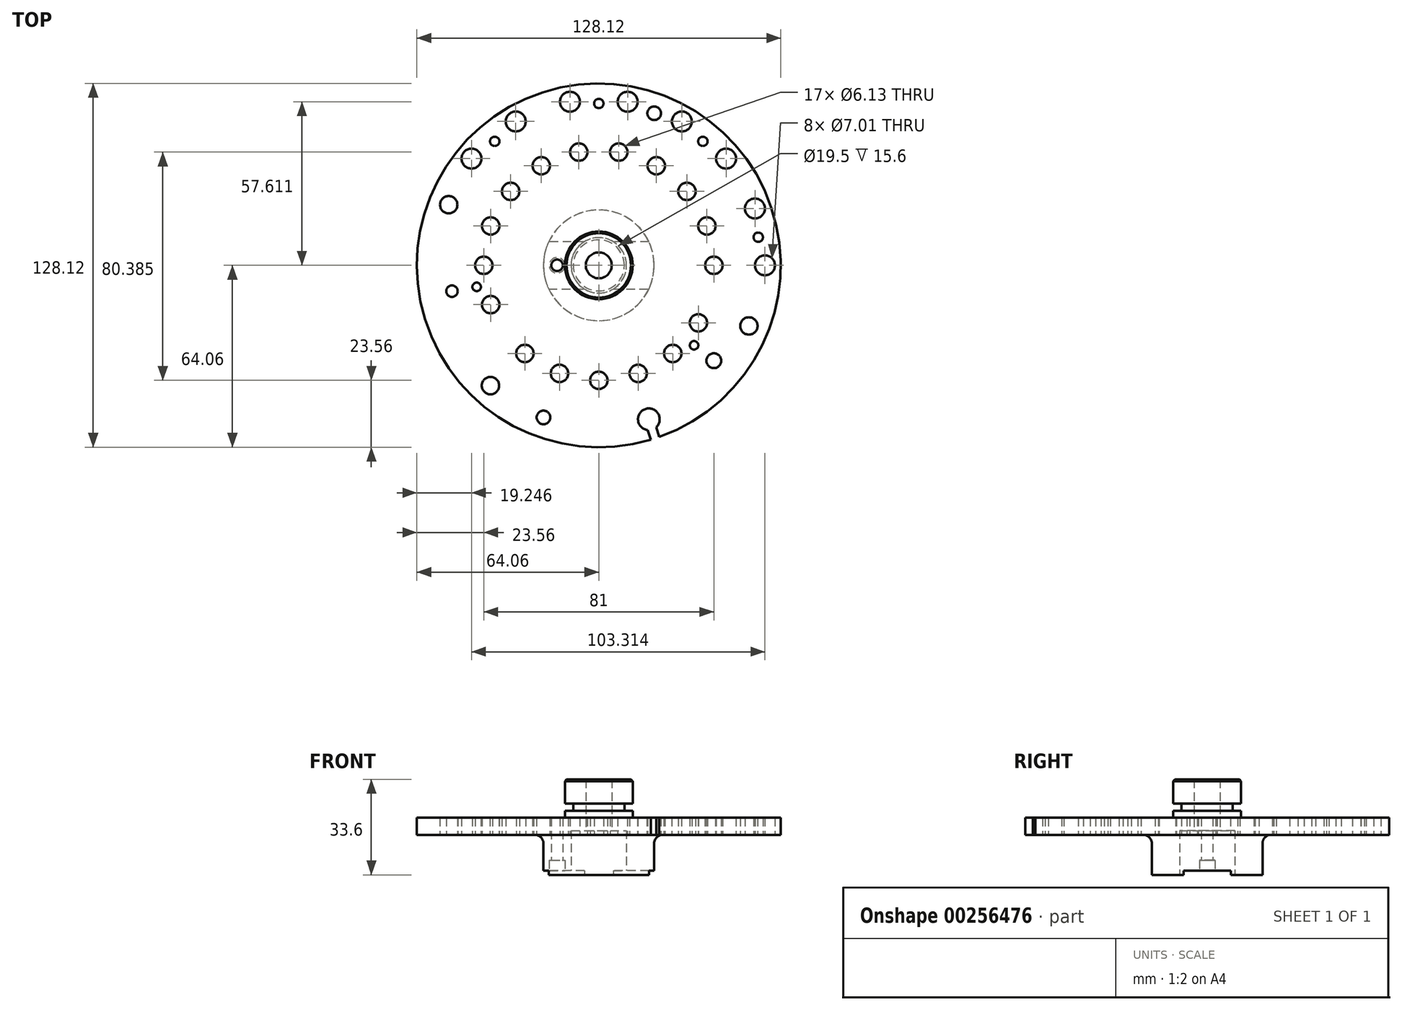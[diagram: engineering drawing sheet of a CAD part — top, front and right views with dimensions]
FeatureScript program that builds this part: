
annotation { "Feature Type Name" : "Feature", "Feature Type Description" : "" }
export const myFeature = defineFeature(function(context is Context, id is Id, definition is map)
    precondition{}
    {
        {
            var Q0;
            Q0=qCreatedBy(makeId("Front.planeOp"),FACE);
            var sketch = newSketch(context, id + "F0", { "sketchPlane" : qUnion([Q0])});
            skLineSegment(sketch, "E0", {"start": v(3.25, 0) * mm, "end": v(6.5, 0) * mm});
            skLineSegment(sketch, "E1", {"start": v(6.5, 0) * mm, "end": v(6.5, 4.7) * mm});
            skLineSegment(sketch, "E2", {"start": v(6.5, 4.7) * mm, "end": v(21.35, 4.7) * mm});
            skLineSegment(sketch, "E3", {"start": v(21.35, 4.7) * mm, "end": v(21.35, 6.7) * mm});
            skLineSegment(sketch, "E4", {"start": v(21.35, 6.7) * mm, "end": v(3.98, 6.7) * mm});
            skLineSegment(sketch, "E5", {"start": v(3.98, 6.7) * mm, "end": v(3.98, 7.5) * mm});
            skLineSegment(sketch, "E6", {"start": v(3.98, 11.2) * mm, "end": v(1.52, 11.2) * mm});
            skLineSegment(sketch, "E7", {"start": v(1.52, 11.2) * mm, "end": v(1.52, 5.2) * mm});
            skLineSegment(sketch, "E8", {"start": v(1.52, 5.2) * mm, "end": v(3.25, 5.2) * mm});
            skLineSegment(sketch, "E9", {"start": v(3.25, 5.2) * mm, "end": v(3.25, 0) * mm});
            skLineSegment(sketch, "E10", {"start": v(3.98, 7.5) * mm, "end": v(3, 7.5) * mm});
            skLineSegment(sketch, "E11", {"start": v(3, 7.5) * mm, "end": v(3, 8.35) * mm});
            skLineSegment(sketch, "E12", {"start": v(3, 8.35) * mm, "end": v(3.98, 8.35) * mm});
            skLineSegment(sketch, "E13", {"start": v(3.98, 8.35) * mm, "end": v(3.98, 11.2) * mm});
            skLineSegment(sketch, "E14", {"start": v(0, 0) * mm, "end": v(0, 11.2) * mm, "construction": true});
            skSolve(sketch);
        }
        {
            var Q0;
            Q0=makeQuery(id+"F0.imprint","IMPRINT",FACE,{"disambiguationData":[TD([[makeQuery(id+"F0.imprint","IMPRINT",EDGE,{"derivedFrom":sQuery(id+"F0.wireOp",EDGE,"E0")}),1.0]])]});
            var Q1;
            Q1=sQuery(id+"F0.wireOp",EDGE,"E14");
            revolve(context, id + "F1", {"entities" : qUnion([Q0]), "axis" : qUnion([Q1]), "revolveType" : RevolveType.FULL});
        }
        {
            var Q0;
            Q0=makeQuery(id+"F1.opRevolve","SWEPT_FACE",FACE,{"disambiguationData":[OSD([sQuery(id+"F0.wireOp",EDGE,"E2")])]});
            var sketch = newSketch(context, id + "F2", { "sketchPlane" : qUnion([Q0])});
            skLineSegment(sketch, "E15", {"start": v(21.35, 0) * mm, "end": v(0, 0) * mm, "construction": true});
            skLineSegment(sketch, "E16", {"start": v(0, 0) * mm, "end": v(20.07, -7.3) * mm, "construction": true});
            skLineSegment(sketch, "E17", {"start": v(0, 0) * mm, "end": v(16.36, -13.73) * mm, "construction": true});
            skLineSegment(sketch, "E18", {"start": v(0, 0) * mm, "end": v(10.68, -18.5) * mm, "construction": true});
            skLineSegment(sketch, "E19", {"start": v(0, 0) * mm, "end": v(3.7, -21.03) * mm, "construction": true});
            skLineSegment(sketch, "E20", {"start": v(0, 0) * mm, "end": v(-3.7, -21.03) * mm, "construction": true});
            skLineSegment(sketch, "E21", {"start": v(0, 0) * mm, "end": v(-10.68, -18.5) * mm, "construction": true});
            skLineSegment(sketch, "E22", {"start": v(0, 0) * mm, "end": v(-16.36, -13.73) * mm, "construction": true});
            skLineSegment(sketch, "E23", {"start": v(0, 0) * mm, "end": v(-20.07, -7.3) * mm, "construction": true});
            skLineSegment(sketch, "E24", {"start": v(0, 0) * mm, "end": v(-21.35, 0) * mm, "construction": true});
            skLineSegment(sketch, "E25", {"start": v(0, 0) * mm, "end": v(-20.07, 7.3) * mm, "construction": true});
            skLineSegment(sketch, "E26", {"start": v(0, 0) * mm, "end": v(18.5, 10.68) * mm, "construction": true});
            skLineSegment(sketch, "E27", {"start": v(0, 0) * mm, "end": v(13.73, 16.36) * mm, "construction": true});
            skLineSegment(sketch, "E28", {"start": v(0, 0) * mm, "end": v(7.3, 20.07) * mm, "construction": true});
            skLineSegment(sketch, "E29", {"start": v(0, 0) * mm, "end": v(0, 21.35) * mm, "construction": true});
            skLineSegment(sketch, "E30", {"start": v(0, 0) * mm, "end": v(-7.3, 20.07) * mm, "construction": true});
            skLineSegment(sketch, "E31", {"start": v(0, 0) * mm, "end": v(-13.73, 16.36) * mm, "construction": true});
            skCircle(sketch, "E32", {"center": v(0, 0) * mm, "radius": 19.5 * mm, "construction": true});
            skCircle(sketch, "E33", {"center": v(0, 0) * mm, "radius": 13.5 * mm, "construction": true});
            skCircle(sketch, "E34", {"center": v(19.5, 0) * mm, "radius": 1.17 * mm});
            skCircle(sketch, "E35", {"center": v(18.32, -6.67) * mm, "radius": 1.17 * mm});
            skCircle(sketch, "E36", {"center": v(14.94, -12.53) * mm, "radius": 1.17 * mm});
            skCircle(sketch, "E37", {"center": v(9.75, -16.89) * mm, "radius": 1.17 * mm});
            skCircle(sketch, "E38", {"center": v(3.39, -19.2) * mm, "radius": 1.17 * mm});
            skCircle(sketch, "E39", {"center": v(-3.39, -19.2) * mm, "radius": 1.17 * mm});
            skCircle(sketch, "E40", {"center": v(-9.75, -16.89) * mm, "radius": 1.17 * mm});
            skCircle(sketch, "E41", {"center": v(-14.94, -12.53) * mm, "radius": 1.17 * mm});
            skCircle(sketch, "E42", {"center": v(-17.62, -7.12) * mm, "radius": 1.02 * mm});
            skCircle(sketch, "E43", {"center": v(11.7, 6.75) * mm, "radius": 1.02 * mm});
            skCircle(sketch, "E44", {"center": v(8.68, 10.34) * mm, "radius": 1.02 * mm});
            skCircle(sketch, "E45", {"center": v(12.69, -4.62) * mm, "radius": 1.02 * mm});
            skCircle(sketch, "E46", {"center": v(13.5, 0) * mm, "radius": 1.02 * mm});
            skCircle(sketch, "E47", {"center": v(10.34, -8.68) * mm, "radius": 1.02 * mm});
            skCircle(sketch, "E48", {"center": v(6.75, -11.7) * mm, "radius": 1.02 * mm});
            skCircle(sketch, "E49", {"center": v(2.34, -13.3) * mm, "radius": 1.02 * mm});
            skCircle(sketch, "E50", {"center": v(-2.34, -13.3) * mm, "radius": 1.02 * mm});
            skCircle(sketch, "E51", {"center": v(-6.75, -11.7) * mm, "radius": 1.02 * mm});
            skCircle(sketch, "E52", {"center": v(-10.34, -8.68) * mm, "radius": 1.02 * mm});
            skCircle(sketch, "E53", {"center": v(-12.69, -4.62) * mm, "radius": 1.02 * mm});
            skCircle(sketch, "E54", {"center": v(-13.5, 0) * mm, "radius": 1.02 * mm});
            skCircle(sketch, "E55", {"center": v(-12.69, 4.62) * mm, "radius": 1.02 * mm});
            skCircle(sketch, "E56", {"center": v(-8.68, 10.34) * mm, "radius": 1.02 * mm});
            skCircle(sketch, "E57", {"center": v(-4.62, 12.69) * mm, "radius": 1.02 * mm});
            skCircle(sketch, "E58", {"center": v(0, 13.5) * mm, "radius": 1.02 * mm});
            skCircle(sketch, "E59", {"center": v(4.62, 12.69) * mm, "radius": 1.02 * mm});
            skLineSegment(sketch, "E60", {"start": v(0, 0) * mm, "end": v(21.03, -3.7) * mm, "construction": true});
            skLineSegment(sketch, "E61", {"start": v(0, 0) * mm, "end": v(13.73, -16.36) * mm, "construction": true});
            skLineSegment(sketch, "E62", {"start": v(0, 0) * mm, "end": v(7.3, -20.07) * mm, "construction": true});
            skLineSegment(sketch, "E63", {"start": v(0, 0) * mm, "end": v(0, -21.35) * mm, "construction": true});
            skLineSegment(sketch, "E64", {"start": v(0, 0) * mm, "end": v(-13.73, -16.36) * mm, "construction": true});
            skCircle(sketch, "E65", {"center": v(18.71, -3.3) * mm, "radius": 0.55 * mm});
            skCircle(sketch, "E66", {"center": v(12.21, -14.55) * mm, "radius": 0.55 * mm});
            skCircle(sketch, "E67", {"center": v(0, -19) * mm, "radius": 0.55 * mm});
            skCircle(sketch, "E68", {"center": v(-12.21, -14.55) * mm, "radius": 0.55 * mm});
            skCircle(sketch, "E69", {"center": v(6.5, -17.85) * mm, "radius": 0.8 * mm});
            skCircle(sketch, "E70", {"center": v(0, 0) * mm, "radius": 19 * mm, "construction": true});
            skLineSegment(sketch, "E71", {"start": v(0, 0) * mm, "end": v(17.62, 7.12) * mm, "construction": true});
            skCircle(sketch, "E72", {"center": v(17.62, 7.12) * mm, "radius": 1.02 * mm});
            skLineSegment(sketch, "E73", {"start": v(0, 0) * mm, "end": v(5.87, 18.07) * mm, "construction": true});
            skArc(sketch, "E74", {"start": v(5.73, 19.33) * mm, "mid": v(5.48, 16.86) * mm, "end": v(6.72, 19.01) * mm});
            skLineSegment(sketch, "E75", {"start": v(5.73, 19.33) * mm, "end": v(6.1, 20.46) * mm});
            skLineSegment(sketch, "E76", {"start": v(6.72, 19.01) * mm, "end": v(7.1, 20.14) * mm});
            skCircle(sketch, "E77", {"center": v(13.5, 11.2) * mm, "radius": 0.87 * mm});
            skCircle(sketch, "E78", {"center": v(11.18, 9.38) * mm, "radius": 0.5 * mm});
            skLineSegment(sketch, "E79", {"start": v(11.18, 9.38) * mm, "end": v(0, 0) * mm, "construction": true});
            skCircle(sketch, "E80", {"center": v(-6.5, 17.85) * mm, "radius": 0.8 * mm});
            skCircle(sketch, "E81", {"center": v(-12.71, 14.12) * mm, "radius": 1.02 * mm});
            skLineSegment(sketch, "E82", {"start": v(0, 0) * mm, "end": v(-12.71, 14.12) * mm, "construction": true});
            skLineSegment(sketch, "E83", {"start": v(0, 0) * mm, "end": v(-17.23, 3.04) * mm, "construction": true});
            skPoint(sketch, "E84", {"position": v(-14.33, 2.53) * mm});
            skCircle(sketch, "E85", {"center": v(-17.23, 3.04) * mm, "radius": 0.68 * mm});
            skCircle(sketch, "E86", {"center": v(-14.33, 2.53) * mm, "radius": 0.5 * mm});
            skLineSegment(sketch, "E87", {"start": v(0, 0) * mm, "end": v(-17.62, -7.12) * mm, "construction": true});
            skSolve(sketch);
        }
        {
            var Q0;
            {Q0=qUnion([makeQuery(id+"F2.imprint","IMPRINT",FACE,{"disambiguationData":[TD([[makeQuery(id+"F2.imprint","IMPRINT",EDGE,{"derivedFrom":sQuery(id+"F2.wireOp",EDGE,"E34")}),1.0]])]}),makeQuery(id+"F2.imprint","IMPRINT",FACE,{"disambiguationData":[TD([[makeQuery(id+"F2.imprint","IMPRINT",EDGE,{"derivedFrom":sQuery(id+"F2.wireOp",EDGE,"E35")}),1.0]])]}),makeQuery(id+"F2.imprint","IMPRINT",FACE,{"disambiguationData":[TD([[makeQuery(id+"F2.imprint","IMPRINT",EDGE,{"derivedFrom":sQuery(id+"F2.wireOp",EDGE,"E36")}),1.0]])]}),makeQuery(id+"F2.imprint","IMPRINT",FACE,{"disambiguationData":[TD([[makeQuery(id+"F2.imprint","IMPRINT",EDGE,{"derivedFrom":sQuery(id+"F2.wireOp",EDGE,"E37")}),1.0]])]}),makeQuery(id+"F2.imprint","IMPRINT",FACE,{"disambiguationData":[TD([[makeQuery(id+"F2.imprint","IMPRINT",EDGE,{"derivedFrom":sQuery(id+"F2.wireOp",EDGE,"E38")}),1.0]])]}),makeQuery(id+"F2.imprint","IMPRINT",FACE,{"disambiguationData":[TD([[makeQuery(id+"F2.imprint","IMPRINT",EDGE,{"derivedFrom":sQuery(id+"F2.wireOp",EDGE,"E39")}),1.0]])]}),makeQuery(id+"F2.imprint","IMPRINT",FACE,{"disambiguationData":[TD([[makeQuery(id+"F2.imprint","IMPRINT",EDGE,{"derivedFrom":sQuery(id+"F2.wireOp",EDGE,"E40")}),1.0]])]}),makeQuery(id+"F2.imprint","IMPRINT",FACE,{"disambiguationData":[TD([[makeQuery(id+"F2.imprint","IMPRINT",EDGE,{"derivedFrom":sQuery(id+"F2.wireOp",EDGE,"E41")}),1.0]])]}),makeQuery(id+"F2.imprint","IMPRINT",FACE,{"disambiguationData":[TD([[makeQuery(id+"F2.imprint","IMPRINT",EDGE,{"derivedFrom":sQuery(id+"F2.wireOp",EDGE,"E42")}),1.0]])]}),makeQuery(id+"F2.imprint","IMPRINT",FACE,{"disambiguationData":[TD([[makeQuery(id+"F2.imprint","IMPRINT",EDGE,{"derivedFrom":sQuery(id+"F2.wireOp",EDGE,"E43")}),1.0]])]}),makeQuery(id+"F2.imprint","IMPRINT",FACE,{"disambiguationData":[TD([[makeQuery(id+"F2.imprint","IMPRINT",EDGE,{"derivedFrom":sQuery(id+"F2.wireOp",EDGE,"E44")}),1.0]])]}),makeQuery(id+"F2.imprint","IMPRINT",FACE,{"disambiguationData":[TD([[makeQuery(id+"F2.imprint","IMPRINT",EDGE,{"derivedFrom":sQuery(id+"F2.wireOp",EDGE,"E45")}),1.0]])]}),makeQuery(id+"F2.imprint","IMPRINT",FACE,{"disambiguationData":[TD([[makeQuery(id+"F2.imprint","IMPRINT",EDGE,{"derivedFrom":sQuery(id+"F2.wireOp",EDGE,"E46")}),1.0]])]}),makeQuery(id+"F2.imprint","IMPRINT",FACE,{"disambiguationData":[TD([[makeQuery(id+"F2.imprint","IMPRINT",EDGE,{"derivedFrom":sQuery(id+"F2.wireOp",EDGE,"E47")}),1.0]])]}),makeQuery(id+"F2.imprint","IMPRINT",FACE,{"disambiguationData":[TD([[makeQuery(id+"F2.imprint","IMPRINT",EDGE,{"derivedFrom":sQuery(id+"F2.wireOp",EDGE,"E48")}),1.0]])]}),makeQuery(id+"F2.imprint","IMPRINT",FACE,{"disambiguationData":[TD([[makeQuery(id+"F2.imprint","IMPRINT",EDGE,{"derivedFrom":sQuery(id+"F2.wireOp",EDGE,"E49")}),1.0]])]}),makeQuery(id+"F2.imprint","IMPRINT",FACE,{"disambiguationData":[TD([[makeQuery(id+"F2.imprint","IMPRINT",EDGE,{"derivedFrom":sQuery(id+"F2.wireOp",EDGE,"E50")}),1.0]])]}),makeQuery(id+"F2.imprint","IMPRINT",FACE,{"disambiguationData":[TD([[makeQuery(id+"F2.imprint","IMPRINT",EDGE,{"derivedFrom":sQuery(id+"F2.wireOp",EDGE,"E51")}),1.0]])]}),makeQuery(id+"F2.imprint","IMPRINT",FACE,{"disambiguationData":[TD([[makeQuery(id+"F2.imprint","IMPRINT",EDGE,{"derivedFrom":sQuery(id+"F2.wireOp",EDGE,"E52")}),1.0]])]}),makeQuery(id+"F2.imprint","IMPRINT",FACE,{"disambiguationData":[TD([[makeQuery(id+"F2.imprint","IMPRINT",EDGE,{"derivedFrom":sQuery(id+"F2.wireOp",EDGE,"E53")}),1.0]])]}),makeQuery(id+"F2.imprint","IMPRINT",FACE,{"disambiguationData":[TD([[makeQuery(id+"F2.imprint","IMPRINT",EDGE,{"derivedFrom":sQuery(id+"F2.wireOp",EDGE,"E54")}),1.0]])]}),makeQuery(id+"F2.imprint","IMPRINT",FACE,{"disambiguationData":[TD([[makeQuery(id+"F2.imprint","IMPRINT",EDGE,{"derivedFrom":sQuery(id+"F2.wireOp",EDGE,"E55")}),1.0]])]}),makeQuery(id+"F2.imprint","IMPRINT",FACE,{"disambiguationData":[TD([[makeQuery(id+"F2.imprint","IMPRINT",EDGE,{"derivedFrom":sQuery(id+"F2.wireOp",EDGE,"E56")}),1.0]])]}),makeQuery(id+"F2.imprint","IMPRINT",FACE,{"disambiguationData":[TD([[makeQuery(id+"F2.imprint","IMPRINT",EDGE,{"derivedFrom":sQuery(id+"F2.wireOp",EDGE,"E57")}),1.0]])]}),makeQuery(id+"F2.imprint","IMPRINT",FACE,{"disambiguationData":[TD([[makeQuery(id+"F2.imprint","IMPRINT",EDGE,{"derivedFrom":sQuery(id+"F2.wireOp",EDGE,"E58")}),1.0]])]}),makeQuery(id+"F2.imprint","IMPRINT",FACE,{"disambiguationData":[TD([[makeQuery(id+"F2.imprint","IMPRINT",EDGE,{"derivedFrom":sQuery(id+"F2.wireOp",EDGE,"E59")}),1.0]])]}),makeQuery(id+"F2.imprint","IMPRINT",FACE,{"disambiguationData":[TD([[makeQuery(id+"F2.imprint","IMPRINT",EDGE,{"derivedFrom":sQuery(id+"F2.wireOp",EDGE,"E65")}),1.0]])]}),makeQuery(id+"F2.imprint","IMPRINT",FACE,{"disambiguationData":[TD([[makeQuery(id+"F2.imprint","IMPRINT",EDGE,{"derivedFrom":sQuery(id+"F2.wireOp",EDGE,"E66")}),1.0]])]}),makeQuery(id+"F2.imprint","IMPRINT",FACE,{"disambiguationData":[TD([[makeQuery(id+"F2.imprint","IMPRINT",EDGE,{"derivedFrom":sQuery(id+"F2.wireOp",EDGE,"E67")}),1.0]])]}),makeQuery(id+"F2.imprint","IMPRINT",FACE,{"disambiguationData":[TD([[makeQuery(id+"F2.imprint","IMPRINT",EDGE,{"derivedFrom":sQuery(id+"F2.wireOp",EDGE,"E68")}),1.0]])]}),makeQuery(id+"F2.imprint","IMPRINT",FACE,{"disambiguationData":[TD([[makeQuery(id+"F2.imprint","IMPRINT",EDGE,{"derivedFrom":sQuery(id+"F2.wireOp",EDGE,"E69")}),1.0]])]}),makeQuery(id+"F2.imprint","IMPRINT",FACE,{"disambiguationData":[TD([[makeQuery(id+"F2.imprint","IMPRINT",EDGE,{"derivedFrom":sQuery(id+"F2.wireOp",EDGE,"E72")}),1.0]])]}),makeQuery(id+"F2.imprint","IMPRINT",FACE,{"disambiguationData":[TD([[makeQuery(id+"F2.imprint","IMPRINT",EDGE,{"derivedFrom":sQuery(id+"F2.wireOp",EDGE,"E77")}),1.0]])]}),makeQuery(id+"F2.imprint","IMPRINT",FACE,{"disambiguationData":[TD([[makeQuery(id+"F2.imprint","IMPRINT",EDGE,{"derivedFrom":sQuery(id+"F2.wireOp",EDGE,"E78")}),1.0]])]}),makeQuery(id+"F2.imprint","IMPRINT",FACE,{"disambiguationData":[TD([[makeQuery(id+"F2.imprint","IMPRINT",EDGE,{"derivedFrom":sQuery(id+"F2.wireOp",EDGE,"E80")}),1.0]])]}),makeQuery(id+"F2.imprint","IMPRINT",FACE,{"disambiguationData":[TD([[makeQuery(id+"F2.imprint","IMPRINT",EDGE,{"derivedFrom":sQuery(id+"F2.wireOp",EDGE,"E81")}),1.0]])]}),makeQuery(id+"F2.imprint","IMPRINT",FACE,{"disambiguationData":[TD([[makeQuery(id+"F2.imprint","IMPRINT",EDGE,{"derivedFrom":sQuery(id+"F2.wireOp",EDGE,"E85")}),1.0]])]}),makeQuery(id+"F2.imprint","IMPRINT",FACE,{"disambiguationData":[TD([[makeQuery(id+"F2.imprint","IMPRINT",EDGE,{"derivedFrom":sQuery(id+"F2.wireOp",EDGE,"E86")}),1.0]])]})]);}
            var Q1;
            Q1=makeQuery(id+"F2.imprint","IMPRINT",FACE,{"disambiguationData":[TD([[makeQuery(id+"F2.imprint","IMPRINT",EDGE,{"derivedFrom":sQuery(id+"F2.wireOp",EDGE,"E74")}),1.0]])]});
            extrude(context, id + "F3", {"entities" : qUnion([Q0, Q1]), "operationType" : NewBodyOperationType.REMOVE, "endBound" : BoundingType.THROUGH_ALL, "oppositeDirection" : true, "depth" : 25 * mm});
        }
        {
            var Q0;
            Q0=makeQuery(id+"F1.opRevolve","SWEPT_EDGE",EDGE,{"disambiguationData":[OSD([sQuery(id+"F0.wireOp",EDGE,"E1"),sQuery(id+"F0.wireOp",EDGE,"E2")])]});
            fillet(context, id + "F4", {"entities" : qUnion([Q0]), "radius" : 1 * mm, "tangentPropagation" : true, "allowEdgeOverflow" : false});
        }
        {
            var Q0;
            Q0=makeQuery(id+"F1.opRevolve","SWEPT_EDGE",EDGE,{"disambiguationData":[OSD([sQuery(id+"F0.wireOp",EDGE,"E4"),sQuery(id+"F0.wireOp",EDGE,"E5")])]});
            fillet(context, id + "F5", {"entities" : qUnion([Q0]), "radius" : 0.2 * mm, "tangentPropagation" : true, "allowEdgeOverflow" : false});
        }
        {
            var Q0;
            Q0=makeQuery(id+"F1.opRevolve","SWEPT_EDGE",EDGE,{"disambiguationData":[OSD([sQuery(id+"F0.wireOp",EDGE,"E6"),sQuery(id+"F0.wireOp",EDGE,"E13")])]});
            chamfer(context, id + "F6", {"entities" : qUnion([Q0]), "width" : 0.2 * mm, "tangentPropagation" : true});
        }
        {
            var Q0;
            Q0=makeQuery(id+"F1.opRevolve","SWEPT_FACE",FACE,{"disambiguationData":[OSD([sQuery(id+"F0.wireOp",EDGE,"E0")])]});
            var sketch = newSketch(context, id + "F7", { "sketchPlane" : qUnion([Q0])});
            skLineSegment(sketch, "E88", {"start": v(5.88, -2.77) * mm, "end": v(-5.88, -2.77) * mm});
            skLineSegment(sketch, "E89", {"start": v(-5.88, 2.77) * mm, "end": v(5.88, 2.77) * mm});
            skSolve(sketch);
        }
        {
            var Q0;
            {var subQ0=sQuery(id+"F0.wireOp",EDGE,"E0");var subQ4=sQuery(id+"F7.wireOp",EDGE,"E88");var subQ6=makeQuery(id+"F1.opRevolve","SWEPT_EDGE",EDGE,{"disambiguationData":[OSD([subQ0,sQuery(id+"F0.wireOp",EDGE,"E1")])]});var subQ8=makeQuery(id+"F7.imprint","INTERSECT",VERTEX,{"disambiguationData":[OD(0.0)],"derivedFrom":[subQ6,subQ4]});Q0=makeQuery(id+"F7.imprint","IMPRINT",FACE,{"disambiguationData":[TD([[makeQuery(id+"F7.imprint","IMPRINT",EDGE,{"disambiguationData":[TD([[subQ8,-1.0]])],"derivedFrom":subQ4}),-1.0]])]});}
            var Q1;
            {var subQ0=sQuery(id+"F0.wireOp",EDGE,"E0");var subQ4=sQuery(id+"F7.wireOp",EDGE,"E88");var subQ6=makeQuery(id+"F1.opRevolve","SWEPT_EDGE",EDGE,{"disambiguationData":[OSD([subQ0,sQuery(id+"F0.wireOp",EDGE,"E1")])]});var subQ8=makeQuery(id+"F7.imprint","INTERSECT",VERTEX,{"disambiguationData":[OD(1.0)],"derivedFrom":[subQ6,subQ4]});Q1=makeQuery(id+"F7.imprint","IMPRINT",FACE,{"disambiguationData":[TD([[makeQuery(id+"F7.imprint","IMPRINT",EDGE,{"disambiguationData":[TD([[subQ8,1.0]])],"derivedFrom":subQ4}),-1.0]])]});}
            extrude(context, id + "F8", {"entities" : qUnion([Q0, Q1]), "operationType" : NewBodyOperationType.REMOVE, "oppositeDirection" : true, "depth" : 0.5 * mm});
        }
        {
            var Q0;
            {var subQ0=sQuery(id+"F0.wireOp",EDGE,"E0");var subQ1=sQuery(id+"F0.wireOp",EDGE,"E1");var subQ2=sQuery(id+"F0.wireOp",EDGE,"E9");var subQ3=sQuery(id+"F7.wireOp",EDGE,"E88");var subQ4=sQuery(id+"F7.wireOp",EDGE,"E89");var subQ5=makeQuery(id+"F1.opRevolve","SWEPT_EDGE",EDGE,{"disambiguationData":[OSD([subQ0,subQ2])]});var subQ6=makeQuery(id+"F7.imprint","INTERSECT",VERTEX,{"disambiguationData":[OD(1.0)],"derivedFrom":[subQ5,subQ3]});var subQ7=makeQuery(id+"F1.opRevolve","SWEPT_EDGE",EDGE,{"disambiguationData":[OSD([subQ0,subQ1])]});var subQ8=makeQuery(id+"F7.imprint","INTERSECT",VERTEX,{"disambiguationData":[OD(1.0)],"derivedFrom":[subQ7,subQ3]});var subQ10=makeQuery(id+"F7.imprint","INTERSECT",VERTEX,{"disambiguationData":[OD(0.0)],"derivedFrom":[subQ7,subQ4]});Q0=makeQuery(id+"F8.boolean.opBoolean","COPY",FACE,{"derivedFrom":makeQuery(id+"F8.opExtrude","CAP_FACE",FACE,{"disambiguationData":[OSD([subQ0,subQ1,subQ2,subQ3,subQ4]),TDD([makeQuery(id+"F7.imprint","IMPRINT",EDGE,{"disambiguationData":[TD([[subQ8,1.0]])],"derivedFrom":subQ3}),makeQuery(id+"F7.imprint","IMPRINT",EDGE,{"disambiguationData":[TD([[subQ10,-1.0]])],"derivedFrom":subQ4}),makeQuery(id+"F7.imprint","IMPRINT",EDGE,{"disambiguationData":[TD([[subQ8,1.0]])],"derivedFrom":subQ7}),makeQuery(id+"F7.imprint","IMPRINT",EDGE,{"disambiguationData":[TD([[subQ6,1.0]])],"derivedFrom":subQ5})])],"isStart":false})});}
            var sketch = newSketch(context, id + "F9", { "sketchPlane" : qUnion([Q0])});
            skCircle(sketch, "E90", {"center": v(-4.9, 0) * mm, "radius": 0.68 * mm});
            skSolve(sketch);
        }
        {
            var Q0;
            Q0=makeQuery(id+"F9.imprint","IMPRINT",FACE,{"disambiguationData":[TD([[makeQuery(id+"F9.imprint","IMPRINT",EDGE,{"derivedFrom":sQuery(id+"F9.wireOp",EDGE,"E90")}),1.0]])]});
            extrude(context, id + "F10", {"entities" : qUnion([Q0]), "operationType" : NewBodyOperationType.REMOVE, "endBound" : BoundingType.THROUGH_ALL, "oppositeDirection" : true, "depth" : 25 * mm});
        }
        {
            var Q0;
            {var subQ0=sQuery(id+"F0.wireOp",EDGE,"E0");var subQ1=sQuery(id+"F0.wireOp",EDGE,"E1");var subQ2=sQuery(id+"F0.wireOp",EDGE,"E9");var subQ3=sQuery(id+"F7.wireOp",EDGE,"E88");var subQ4=sQuery(id+"F7.wireOp",EDGE,"E89");var subQ5=makeQuery(id+"F1.opRevolve","SWEPT_EDGE",EDGE,{"disambiguationData":[OSD([subQ0,subQ2])]});var subQ6=makeQuery(id+"F7.imprint","INTERSECT",VERTEX,{"disambiguationData":[OD(1.0)],"derivedFrom":[subQ5,subQ3]});var subQ7=makeQuery(id+"F1.opRevolve","SWEPT_EDGE",EDGE,{"disambiguationData":[OSD([subQ0,subQ1])]});var subQ8=makeQuery(id+"F7.imprint","INTERSECT",VERTEX,{"disambiguationData":[OD(1.0)],"derivedFrom":[subQ7,subQ3]});var subQ10=makeQuery(id+"F7.imprint","INTERSECT",VERTEX,{"disambiguationData":[OD(0.0)],"derivedFrom":[subQ7,subQ4]});Q0=makeQuery(id+"F8.boolean.opBoolean","COPY",FACE,{"derivedFrom":makeQuery(id+"F8.opExtrude","CAP_FACE",FACE,{"disambiguationData":[OSD([subQ0,subQ1,subQ2,subQ3,subQ4]),TDD([makeQuery(id+"F7.imprint","IMPRINT",EDGE,{"disambiguationData":[TD([[subQ8,1.0]])],"derivedFrom":subQ3}),makeQuery(id+"F7.imprint","IMPRINT",EDGE,{"disambiguationData":[TD([[subQ10,-1.0]])],"derivedFrom":subQ4}),makeQuery(id+"F7.imprint","IMPRINT",EDGE,{"disambiguationData":[TD([[subQ8,1.0]])],"derivedFrom":subQ7}),makeQuery(id+"F7.imprint","IMPRINT",EDGE,{"disambiguationData":[TD([[subQ6,1.0]])],"derivedFrom":subQ5})])],"isStart":false})});}
            var sketch = newSketch(context, id + "F11", { "sketchPlane" : qUnion([Q0])});
            skCircle(sketch, "E91", {"center": v(-4.9, 0) * mm, "radius": 0.92 * mm});
            skSolve(sketch);
        }
        {
            var Q0;
            {var subQ0=makeQuery(id+"F11.imprint","IMPRINT",EDGE,{"derivedFrom":makeQuery(id+"F10.boolean.opBoolean","COPY",EDGE,{"derivedFrom":makeQuery(id+"F10.opExtrude","CAP_EDGE",EDGE,{"disambiguationData":[OSD([sQuery(id+"F9.wireOp",EDGE,"E90")])],"isStart":true})})});Q0=qUnion([makeQuery(id+"F11.imprint","IMPRINT",FACE,{"disambiguationData":[TD([[subQ0,1.0]])]}),makeQuery(id+"F11.imprint","IMPRINT",FACE,{"disambiguationData":[TD([[makeQuery(id+"F11.imprint","IMPRINT",EDGE,{"derivedFrom":sQuery(id+"F11.wireOp",EDGE,"E91")}),1.0]])]})]);}
            extrude(context, id + "F12", {"entities" : qUnion([Q0]), "operationType" : NewBodyOperationType.REMOVE, "oppositeDirection" : true, "depth" : 1.2 * mm});
        }
        {
            var Q0;
            Q0=makeQuery(id+"F1.opRevolve","SWEPT_BODY",BODY,{"disambiguationData":[OSD([sQuery(id+"F0.wireOp",EDGE,"E0"),sQuery(id+"F0.wireOp",EDGE,"E1"),sQuery(id+"F0.wireOp",EDGE,"E2"),sQuery(id+"F0.wireOp",EDGE,"E3"),sQuery(id+"F0.wireOp",EDGE,"E4"),sQuery(id+"F0.wireOp",EDGE,"E5"),sQuery(id+"F0.wireOp",EDGE,"E6"),sQuery(id+"F0.wireOp",EDGE,"E7"),sQuery(id+"F0.wireOp",EDGE,"E8"),sQuery(id+"F0.wireOp",EDGE,"E9"),sQuery(id+"F0.wireOp",EDGE,"E10"),sQuery(id+"F0.wireOp",EDGE,"E11"),sQuery(id+"F0.wireOp",EDGE,"E12"),sQuery(id+"F0.wireOp",EDGE,"E13")])]});
            var Q1;
            Q1=qCreatedBy(makeId("Origin.pointOp"),VERTEX);
            transform(context, id + "F13", {"entities" : qUnion([Q0]), "transformType" : TransformType.SCALE_UNIFORMLY, "scale" : 3, "makeCopy" : false, "scalePoint" : qUnion([Q1])});
        }
    });
